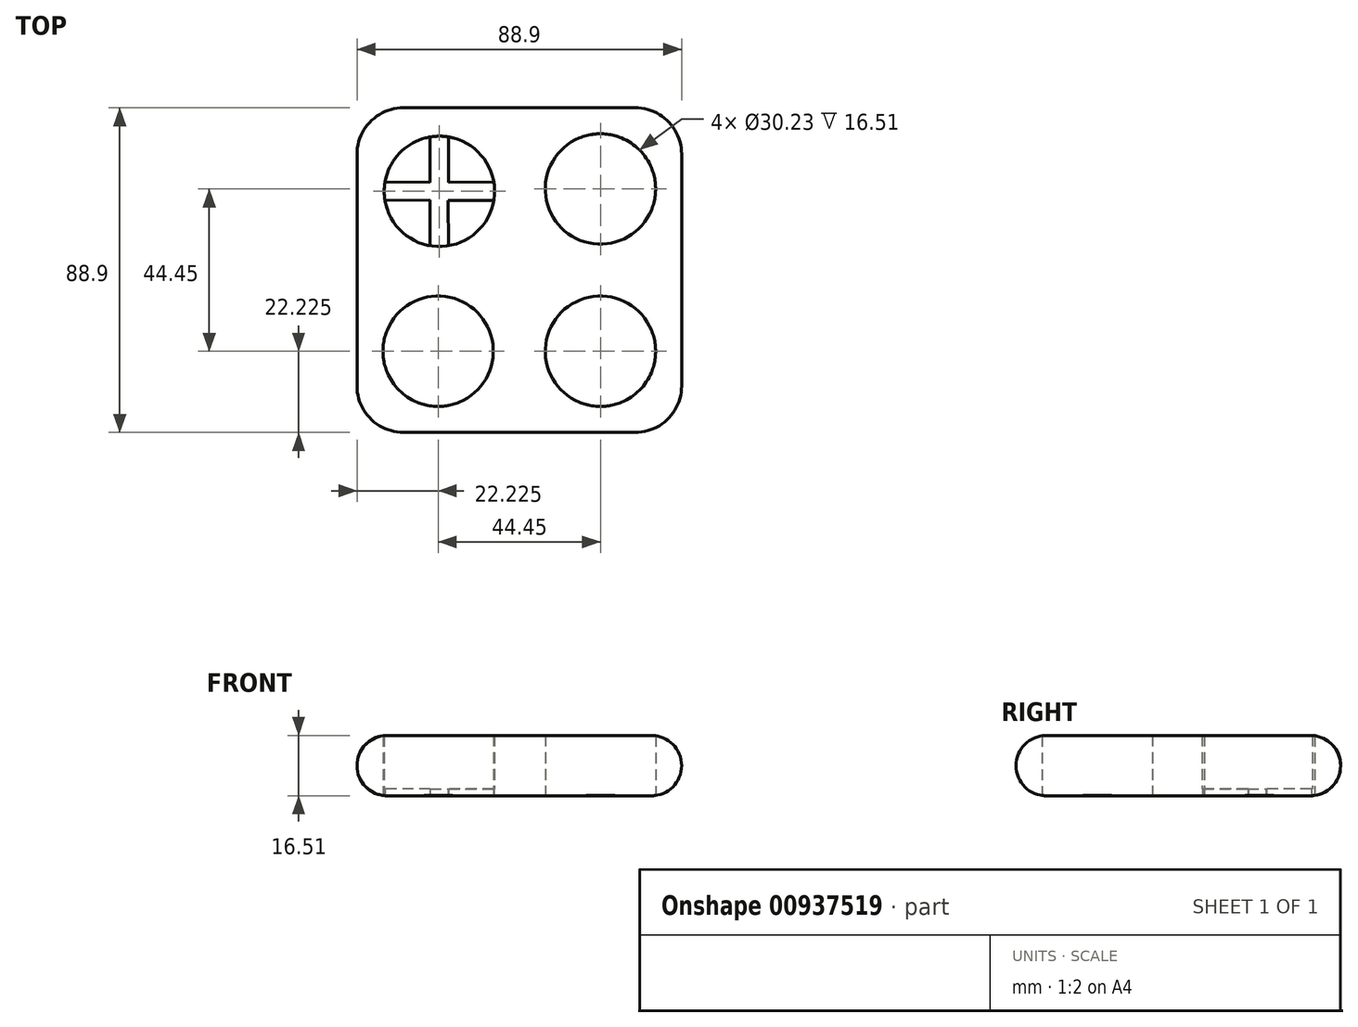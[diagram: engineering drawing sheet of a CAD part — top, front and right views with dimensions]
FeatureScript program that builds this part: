
annotation { "Feature Type Name" : "Feature", "Feature Type Description" : "" }
export const myFeature = defineFeature(function(context is Context, id is Id, definition is map)
    precondition{}
    {
        {
            var Q0;
            Q0=qCreatedBy(makeId("Top.planeOp"),FACE);
            var sketch = newSketch(context, id + "F0", { "sketchPlane" : qUnion([Q0])});
            skLineSegment(sketch, "E0.bottom", {"start": v(-31.75, 44.45) * mm, "end": v(31.75, 44.45) * mm});
            skLineSegment(sketch, "E0.top", {"start": v(-31.75, -44.45) * mm, "end": v(31.75, -44.45) * mm});
            skLineSegment(sketch, "E0.left", {"start": v(-44.45, 31.75) * mm, "end": v(-44.45, -31.75) * mm});
            skLineSegment(sketch, "E0.right", {"start": v(44.45, 31.75) * mm, "end": v(44.45, -31.75) * mm});
            skPoint(sketch, "E1", {"position": v(-21.88, 21.57) * mm});
            skPoint(sketch, "E2", {"position": v(22.22, 22.23) * mm});
            skPoint(sketch, "E3", {"position": v(22.22, -22.22) * mm});
            skPoint(sketch, "E4", {"position": v(-22.23, -22.22) * mm});
            skCircle(sketch, "E5", {"center": v(-21.88, 21.57) * mm, "radius": 15.11 * mm});
            skCircle(sketch, "E6", {"center": v(22.22, 22.23) * mm, "radius": 15.11 * mm});
            skCircle(sketch, "E7", {"center": v(-22.23, -22.22) * mm, "radius": 15.11 * mm});
            skCircle(sketch, "E8", {"center": v(22.22, -22.22) * mm, "radius": 15.11 * mm});
            skPoint(sketch, "E9.visualSharp", {"position": v(-44.45, 44.45) * mm});
            skArc(sketch, "E9.filletArc", {"start": v(-31.75, 44.45) * mm, "mid": v(-40.73, 40.73) * mm, "end": v(-44.45, 31.75) * mm});
            skPoint(sketch, "E10.visualSharp", {"position": v(44.45, 44.45) * mm});
            skArc(sketch, "E10.filletArc", {"start": v(44.45, 31.75) * mm, "mid": v(40.73, 40.73) * mm, "end": v(31.75, 44.45) * mm});
            skPoint(sketch, "E11.visualSharp", {"position": v(44.45, -44.45) * mm});
            skArc(sketch, "E11.filletArc", {"start": v(31.75, -44.45) * mm, "mid": v(40.73, -40.73) * mm, "end": v(44.45, -31.75) * mm});
            skPoint(sketch, "E12.visualSharp", {"position": v(-44.45, -44.45) * mm});
            skArc(sketch, "E12.filletArc", {"start": v(-44.45, -31.75) * mm, "mid": v(-40.73, -40.73) * mm, "end": v(-31.75, -44.45) * mm});
            skCircle(sketch, "E13", {"center": v(-21.88, 21.57) * mm, "radius": 3.5 * mm});
            skCircle(sketch, "E14", {"center": v(22.22, 22.23) * mm, "radius": 3.5 * mm});
            skCircle(sketch, "E15", {"center": v(-22.23, -22.22) * mm, "radius": 3.5 * mm});
            skCircle(sketch, "E16", {"center": v(22.22, -22.22) * mm, "radius": 3.5 * mm});
            skPoint(sketch, "E17", {"position": v(-21.88, 36.68) * mm});
            skPoint(sketch, "E18", {"position": v(-37, 21.57) * mm});
            skPoint(sketch, "E19", {"position": v(-21.88, 6.45) * mm});
            skPoint(sketch, "E20", {"position": v(-6.77, 21.57) * mm});
            skPoint(sketch, "E21", {"position": v(-24.4, 36.47) * mm});
            skPoint(sketch, "E22", {"position": v(-19.35, 36.47) * mm});
            skPoint(sketch, "E23", {"position": v(-6.98, 24.1) * mm});
            skPoint(sketch, "E24", {"position": v(-6.98, 19.04) * mm});
            skPoint(sketch, "E25", {"position": v(-19.35, 6.67) * mm});
            skPoint(sketch, "E26", {"position": v(-36.78, 19.04) * mm});
            skPoint(sketch, "E27", {"position": v(-36.78, 24.1) * mm});
            skLineSegment(sketch, "E28", {"start": v(-24.4, 36.47) * mm, "end": v(-24.4, 23.97) * mm});
            skLineSegment(sketch, "E29", {"start": v(-19.35, 36.47) * mm, "end": v(-19.35, 23.97) * mm});
            skLineSegment(sketch, "E30", {"start": v(-19.35, 23.97) * mm, "end": v(-6.98, 24.1) * mm});
            skLineSegment(sketch, "E31", {"start": v(-6.98, 19.04) * mm, "end": v(-19.47, 19.04) * mm});
            skPoint(sketch, "E32", {"position": v(-24.4, 6.67) * mm});
            skLineSegment(sketch, "E33", {"start": v(-19.47, 19.04) * mm, "end": v(-19.35, 6.67) * mm});
            skLineSegment(sketch, "E34", {"start": v(-24.4, 6.67) * mm, "end": v(-24.4, 19.16) * mm});
            skLineSegment(sketch, "E35", {"start": v(-24.4, 19.16) * mm, "end": v(-36.78, 19.04) * mm});
            skLineSegment(sketch, "E36", {"start": v(-24.4, 23.97) * mm, "end": v(-36.78, 24.1) * mm});
            skSolve(sketch);
        }
        {
            var Q0;
            Q0=makeQuery(id+"F0.imprint","IMPRINT",FACE,{"disambiguationData":[TD([[makeQuery(id+"F0.imprint","IMPRINT",EDGE,{"derivedFrom":sQuery(id+"F0.wireOp",EDGE,"E0.bottom")}),-1.0]])]});
            extrude(context, id + "F1", {"entities" : qUnion([Q0]), "depth" : 16.5 * mm, "offsetDistance" : 25.4 * mm});
        }
        {
            var Q0;
            {var subQ0=sQuery(id+"F0.wireOp",EDGE,"E30");Q0=makeQuery(id+"F0.imprint","IMPRINT",FACE,{"disambiguationData":[TD([[makeQuery(id+"F0.imprint","IMPRINT",EDGE,{"derivedFrom":subQ0}),-1.0]])]});}
            var Q1;
            {var subQ0=sQuery(id+"F0.wireOp",EDGE,"E28");Q1=makeQuery(id+"F0.imprint","IMPRINT",FACE,{"disambiguationData":[TD([[makeQuery(id+"F0.imprint","IMPRINT",EDGE,{"derivedFrom":subQ0}),1.0]])]});}
            var Q2;
            {var subQ0=sQuery(id+"F0.wireOp",EDGE,"E13");var subQ1=makeQuery(id+"F0.imprint","INTERSECT",VERTEX,{"derivedFrom":[subQ0,sQuery(id+"F0.wireOp",EDGE,"E28"),sQuery(id+"F0.wireOp",EDGE,"E36")]});Q2=makeQuery(id+"F0.imprint","IMPRINT",FACE,{"disambiguationData":[TD([[makeQuery(id+"F0.imprint","IMPRINT",EDGE,{"disambiguationData":[TD([[subQ1,1.0]])],"derivedFrom":subQ0}),1.0]])]});}
            var Q3;
            {var subQ0=sQuery(id+"F0.wireOp",EDGE,"E35");Q3=makeQuery(id+"F0.imprint","IMPRINT",FACE,{"disambiguationData":[TD([[makeQuery(id+"F0.imprint","IMPRINT",EDGE,{"derivedFrom":subQ0}),-1.0]])]});}
            var Q4;
            {var subQ0=sQuery(id+"F0.wireOp",EDGE,"E33");Q4=makeQuery(id+"F0.imprint","IMPRINT",FACE,{"disambiguationData":[TD([[makeQuery(id+"F0.imprint","IMPRINT",EDGE,{"derivedFrom":subQ0}),-1.0]])]});}
            extrude(context, id + "F2", {"entities" : qUnion([Q0, Q1, Q2, Q3, Q4]), "operationType" : NewBodyOperationType.ADD, "depth" : 1.9 * mm, "offsetDistance" : 25.4 * mm});
        }
        {
            var Q0;
            Q0=makeQuery(id+"F1.opExtrude","CAP_EDGE",EDGE,{"disambiguationData":[OSD([sQuery(id+"F0.wireOp",EDGE,"E9.filletArc")])],"isStart":false});
            var Q1;
            Q1=makeQuery(id+"F1.opExtrude","CAP_EDGE",EDGE,{"disambiguationData":[OSD([sQuery(id+"F0.wireOp",EDGE,"E0.left")])],"isStart":false});
            var Q2;
            Q2=makeQuery(id+"F1.opExtrude","CAP_EDGE",EDGE,{"disambiguationData":[OSD([sQuery(id+"F0.wireOp",EDGE,"E0.top")])],"isStart":true});
            fillet(context, id + "F3", {"entities" : qUnion([Q0, Q1, Q2]), "radius" : 8.25 * mm, "tangentPropagation" : true, "allowEdgeOverflow" : false});
        }
    });
